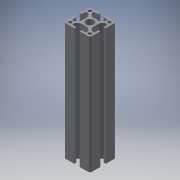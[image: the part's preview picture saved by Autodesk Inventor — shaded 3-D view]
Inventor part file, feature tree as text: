
AUTODESK INVENTOR PART (.ipt)
format: ipt  version: 2018 (Build 220112000, 112)  size: 201,728 bytes
history: native  units: mm
features: other x42, sketch x5, hole x4, extrude x1
ambient origin geometry x8: Origin, YZ Plane, XZ Plane, XY Plane, X Axis, Y Axis, Z Axis, Center Point
bodies: Solid1 (feature_tree)
feature tree (52):
  extrude  "Extrusion1"  [1 undecoded]
  hole  "Drilling 1"  [1 undecoded]
  hole  "Drilling 2"  [1 undecoded]
  hole  "Drilling 3"  [1 undecoded]
  hole  "Drilling 4"  [1 undecoded]
  other  "side_4d_XY"
  other  "side_4d_YZ"
  other  "side_4d_ZX"
  other  "side_4d_X"
  other  "side_4d_Y"
  other  "side_4d_Z"
  other  "side_4d_Center"
  other  "side_1a_XY"
  other  "side_1a_YZ"
  other  "side_1a_ZX"
  other  "side_1a_X"
  other  "side_1a_Y"
  other  "side_1a_Z"
  other  "side_1a_Center"
  other  "side_2b_XY"
  other  "side_2b_YZ"
  other  "side_2b_ZX"
  other  "side_2b_X"
  other  "side_2b_Y"
  other  "side_2b_Z"
  other  "side_2b_Center"
  other  "side_3c_XY"
  other  "side_3c_YZ"
  other  "side_3c_ZX"
  other  "side_3c_X"
  other  "side_3c_Y"
  other  "side_3c_Z"
  other  "side_3c_Center"
  other  "end_XY"
  other  "end_YZ"
  other  "end_ZX"
  other  "end_X"
  other  "end_Y"
  other  "end_Z"
  other  "end_Center"
  other  "start_XY"
  other  "start_YZ"
  other  "start_ZX"
  other  "start_X"
  other  "start_Y"
  other  "start_Z"
  other  "start_Center"
  sketch  "Skizze_1"  dims[d0=180.0mm d1=0.0mm]
  sketch  "Sketch2"  dims[d2=5.0mm d3=6.0mm d4=4.0mm d5=2.0mm d6=90.0deg d7=6000.0mm d8=0.0mm]
  sketch  "Sketch3"  dims[d9=5.0mm d10=6.0mm d11=4.0mm d12=2.0mm d13=90.0deg d14=6000.0mm d15=0.0mm]
  sketch  "Sketch4"  dims[d16=5.0mm d17=6.0mm d18=4.0mm d19=2.0mm d20=90.0deg d21=6000.0mm d22=0.0mm]
  sketch  "Sketch5"  dims[d23=5.0mm d24=6.0mm d25=4.0mm d26=2.0mm d27=90.0deg d28=6000.0mm d29=0.0mm]
note: 5 required parameter values undecoded (feature->parameter linkage not recoverable at this tier; creation-order binding heuristic only, values carry confidence <= 0.55)
